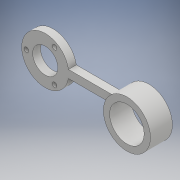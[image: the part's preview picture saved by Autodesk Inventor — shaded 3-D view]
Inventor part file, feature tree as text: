
AUTODESK INVENTOR PART (.ipt)
format: ipt  version: 2017 SP1 (Build 210196100, 196)  size: 142,336 bytes
history: native  units: mm
features: sketch x4, extrude x3, hole x1
ambient origin geometry x8: Origin, YZ Plane, XZ Plane, XY Plane, X Axis, Y Axis, Z Axis, Center Point
bodies: Solide1 (feature_tree)
feature tree (8):
  extrude  "Extrusion1"  Depth=30.0mm
  hole  "Perçage1"  [1 undecoded]
  extrude  "Extrusion2"  Depth=5.0mm TaperAngle=0.0deg
  extrude  "Extrusion3"  Depth=12.0mm
  sketch  "Esquisse1"
  sketch  "Esquisse2"
  sketch  "Esquisse3"
  sketch  "Esquisse4"
note: 1 required parameter value undecoded (feature->parameter linkage not recoverable at this tier; creation-order binding heuristic only, values carry confidence <= 0.55)
